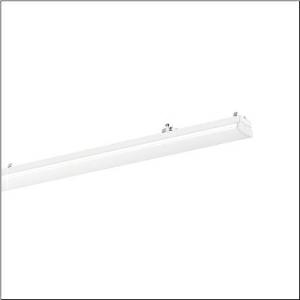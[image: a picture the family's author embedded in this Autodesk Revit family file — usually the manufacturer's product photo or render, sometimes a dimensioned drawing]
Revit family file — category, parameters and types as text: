
# Revit family: licross_21_recessed_opal_mo_52te1d7n48xg
name_source: partatom
category: Lighting Fixtures
units: mm (PartAtom-declared; Revit-internal decimal feet)

## family parameters
Cut with Voids When Loaded = No
Host = Face
Light Source = No
Part Type = Normal
Room Calculation Point = No
Round Connector Dimension = Use Diameter
Shared = No

## types (1)
- Licross 21 recessed opal MO (1 x LED, 8360 lm, 47.9 W, 4000K)
    Apparent Load = 48 VA
    CIE Flux Codes = 44 73 91 87 100
    Color Rendering = 80
    Color Temperature = 4000K
    Default Elevation = 1800 mm
    Description = Licross 21 recessed opal MO, luminaire insert, of sheet steel, galvanised, coil coated, white, length: 1.500mm, width: 66mm, height: 67mm, LED rated luminous flux: 8.360lm, light colour: 840, SDCM (Standard Deviation of Colour Matching)MacAdam ≤ 3 SDCM (initial), control gear: ON/OFF, with plug, 3-pole, with phase selection, mains connection: 220..240V, AC, 50/60Hz, rated input power: 48W, internal wiring halogen-free, primary optical cover: cover, of PMMA, light emission: direct with ceiling illumination distribution, primary light characteristic: symmetric, protection rating (complete): IP54, insulation class (complete): insulation class I (protective earthing), certification: CE, ENEC, VDE, UKCA, protection symbol: D if used in an environment with non-conductive dust loads with corresponding accessories, impact resistance: IK06, permissible ambient temperature for indoor applications: -35..+40°C, corresponds to IFS (International Featured Standards) requirements for safety and quality in the food industry, reducing of maximum allowable ambient temperature of 5°C with ceiling mounting, LABS conformity tested according to VDMA 24364:2018-05, The light source and the operating device comply with the requirements of the Ecodesign Regulation (EU) 2019/2020 and are replaceable in accordance with this regulation, packaging unit: 1 piece
    Height = 83 mm
    Lamp = 1 x LED
    Lamp Light Flux = 8360 lm
    Lamp Power = 47.9 W
    Lamp count = 1
    Length = 1500 mm
    Luminous efficacy = 175 lm/W
    Manufacturer = Siteco
    ModVariant = No
    Model = 52TE1D7N48XG
    Mounting Place = Ceiling
    Mounting Type = Pendant
    Number of Poles = 1
    OnlyDefault = Yes
    Power Factor = 1
    Product Name = Licross 21 recessed opal MO
    Product group = luminaire insert | ceiling pendant
    ProductGroupID = 901
    Protection Class = Protection class I
    Protection Degree = IP 54
    RLX_Detail_Level = 1
    RLX_Emergency_Light_Flux = 0 lm
    RLX_Emergency_Type = 0
    RLX_Emergency_Type_DB = No
    RlxData = <blob elided: 23297 chars, md5=32948a5f>
    Socket = socket
    Standby Power = 0 W
    System Light Flux = 8360 lm
    System Power = 48 W
    Type Comments = Product without accessories
    Type Image = l_1313666.jpg
    URL = http://relux.com
    VarID = ---
    Voltage = 0 V
    Weight = 0.00 kg
    Width = 76 mm

## geometry (parser evidence)
native form markers: Blend x4, Sweep x13
no freeform markers — native parametric forms only
